# Revit family: C_ESCRFTC100X350_2DO_Cad_MULT_Prod
name_source: partatom
category: Detail Items
revit_build: Autodesk Revit 2014 (Build: 20130308_1515(x64)
units: mm (PartAtom-declared; Revit-internal decimal feet)

## types (2) — shared parameters
Density = 0.02 kg
Description = Screws
EPD = https://www.strongtie.eu
ETA / DoP = https://www.strongtie.eu
Manufacturer = Simpson Strong-Tie
Model = ESCRFTC10.0X350
Model Disclaimer = Contact Simpson Strong-Tie Company  for more information
Model ID = 0182178044543470030668714057257587523633
Name = ESCRFTC10.0X350
ObjectType = ESCRFTC10.0X350
Product Material = ElectroGalvanised
Product Type = Screws
Reference = ESCRFTC10.0X350
Technical datasheet = https://www.strongtie.eu
URL = www.strongtie.eu
UniClass Number = Wood screws
UniClass Title = Pr_20_29_76_98

## per-type parameters (varying)
| type | _visiblefront | _visibletop |
| SST_ESCRFTC100X350_Front | Yes | No |
| SST_ESCRFTC100X350_Top | No | Yes |

## geometry (parser evidence)
native form markers: Sweep x1
no freeform markers — native parametric forms only
